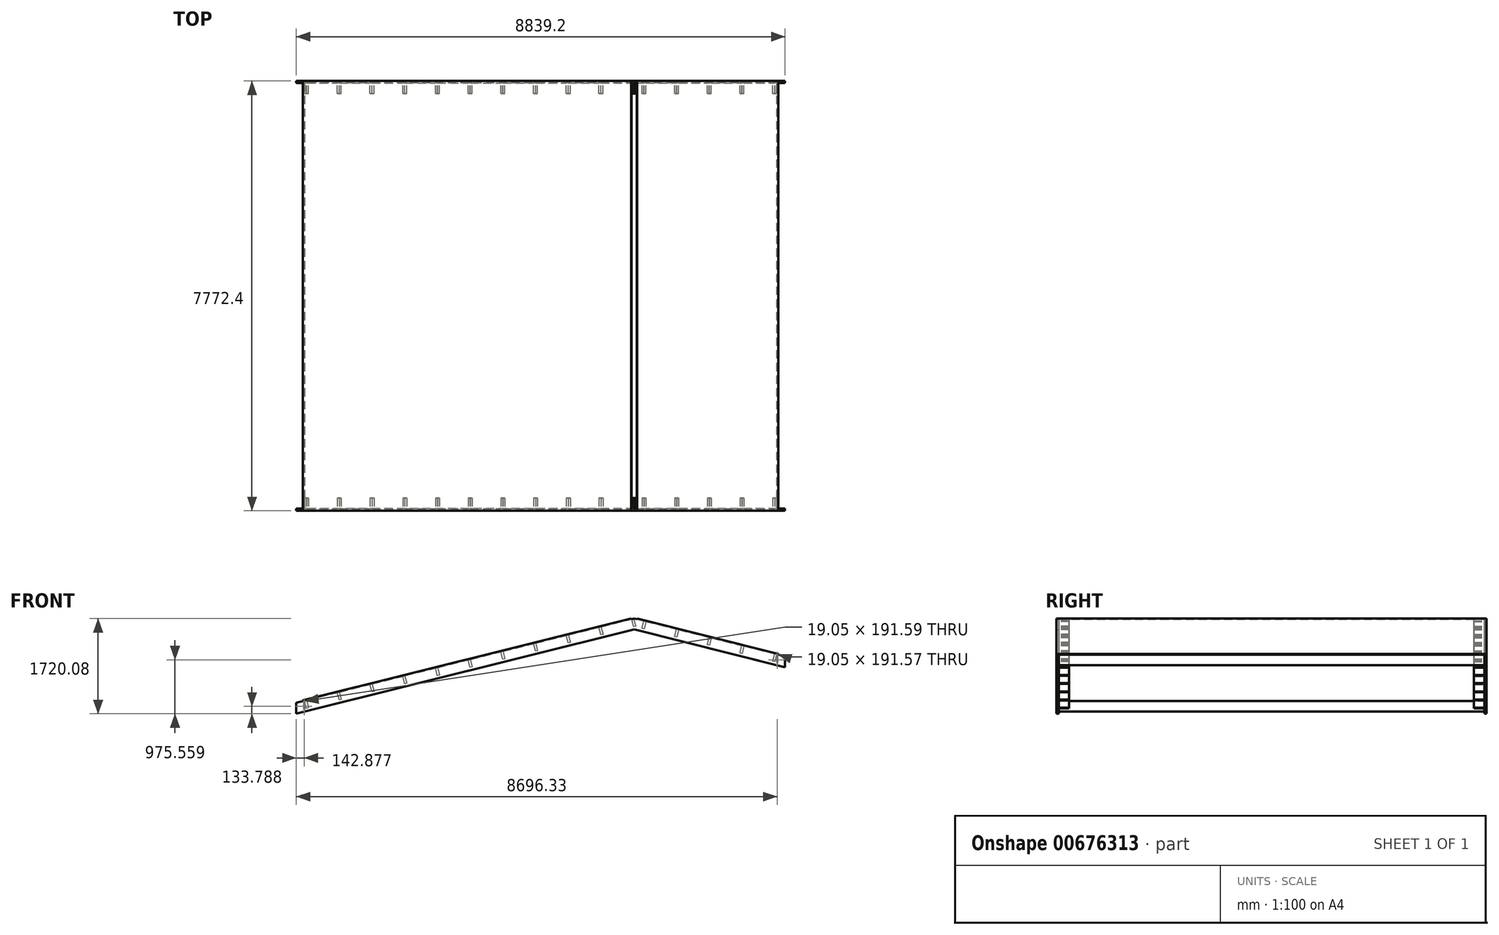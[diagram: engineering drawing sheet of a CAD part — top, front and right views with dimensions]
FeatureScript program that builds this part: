
annotation { "Feature Type Name" : "Feature", "Feature Type Description" : "" }
export const myFeature = defineFeature(function(context is Context, id is Id, definition is map)
    precondition{}
    {
        {
            var Q0;
            Q0=qCreatedBy(makeId("Front.planeOp"),FACE);
            var sketch = newSketch(context, id + "F0", { "sketchPlane" : qUnion([Q0])});
            skLineSegment(sketch, "E0", {"start": v(-6111.16, -1327.32) * mm, "end": v(0, 196.36) * mm});
            skLineSegment(sketch, "E1", {"start": v(0, 196.36) * mm, "end": v(2728.04, -485.65) * mm});
            skLineSegment(sketch, "E2", {"start": v(2728.04, -485.65) * mm, "end": v(2728.04, -682) * mm});
            skLineSegment(sketch, "E3", {"start": v(2728.04, -682) * mm, "end": v(1966.04, -491.5) * mm});
            skLineSegment(sketch, "E4", {"start": v(0, 0) * mm, "end": v(-5209.46, -1298.86) * mm});
            skLineSegment(sketch, "E5", {"start": v(-6111.16, -1523.68) * mm, "end": v(-6111.16, -1327.32) * mm});
            skLineSegment(sketch, "E6", {"start": v(0, 196.36) * mm, "end": v(0, 0) * mm, "construction": true});
            skLineSegment(sketch, "E7", {"start": v(0, 0) * mm, "end": v(46.2, 184.81) * mm, "construction": true});
            skLineSegment(sketch, "E8.trimOffspring", {"start": v(-5349.16, -1333.7) * mm, "end": v(-6111.16, -1523.68) * mm});
            skLineSegment(sketch, "E9.trimOffspring", {"start": v(1826.34, -456.58) * mm, "end": v(0, 0) * mm});
            skLineSegment(sketch, "E10", {"start": v(1966.04, -491.5) * mm, "end": v(1966.04, -456.58) * mm, "construction": true});
            skLineSegment(sketch, "E11", {"start": v(1966.04, -456.58) * mm, "end": v(1826.34, -456.58) * mm, "construction": true});
            skLineSegment(sketch, "E12", {"start": v(-5349.16, -1333.7) * mm, "end": v(-5349.16, -1298.86) * mm, "construction": true});
            skLineSegment(sketch, "E13", {"start": v(-5349.16, -1298.86) * mm, "end": v(-5209.46, -1298.86) * mm, "construction": true});
            skLineSegment(sketch, "E14.bottom", {"start": v(-5349.16, -1298.86) * mm, "end": v(-1831.26, -1298.86) * mm, "construction": true});
            skLineSegment(sketch, "E14.top", {"start": v(-5349.16, -4042.06) * mm, "end": v(-1831.26, -4042.06) * mm, "construction": true});
            skLineSegment(sketch, "E14.left", {"start": v(-5349.16, -1298.86) * mm, "end": v(-5349.16, -4042.06) * mm, "construction": true});
            skLineSegment(sketch, "E14.right", {"start": v(-1831.26, -1298.86) * mm, "end": v(-1831.26, -4042.06) * mm, "construction": true});
            skLineSegment(sketch, "E15.bottom", {"start": v(1966.04, -456.58) * mm, "end": v(-1831.26, -456.58) * mm, "construction": true});
            skLineSegment(sketch, "E15.top", {"start": v(1966.04, -4042.06) * mm, "end": v(-1831.26, -4042.06) * mm, "construction": true});
            skLineSegment(sketch, "E15.left", {"start": v(1966.04, -456.58) * mm, "end": v(1966.04, -4042.06) * mm, "construction": true});
            skLineSegment(sketch, "E15.right", {"start": v(-1831.26, -456.58) * mm, "end": v(-1831.26, -4042.06) * mm, "construction": true});
            skLineSegment(sketch, "E16", {"start": v(-5349.16, -1333.7) * mm, "end": v(-5209.46, -1298.86) * mm});
            skLineSegment(sketch, "E17", {"start": v(1826.34, -456.58) * mm, "end": v(1966.04, -491.5) * mm});
            skSolve(sketch);
        }
        {
            var Q0;
            Q0=qSketchRegion(id+"F0",true);
            extrude(context, id + "F1", {"entities" : qUnion([Q0]), "depth" : 38.1 * mm, "offsetDistance" : 25.4 * mm});
        }
        {
            var Q0;
            Q0=makeQuery(id+"F1.opExtrude","CAP_FACE",FACE,{"disambiguationData":[OSD([sQuery(id+"F0.wireOp",EDGE,"E0"),sQuery(id+"F0.wireOp",EDGE,"E1"),sQuery(id+"F0.wireOp",EDGE,"E2"),sQuery(id+"F0.wireOp",EDGE,"E3"),sQuery(id+"F0.wireOp",EDGE,"E4"),sQuery(id+"F0.wireOp",EDGE,"E5"),sQuery(id+"F0.wireOp",EDGE,"E8.trimOffspring"),sQuery(id+"F0.wireOp",EDGE,"E9.trimOffspring"),sQuery(id+"F0.wireOp",EDGE,"E16"),sQuery(id+"F0.wireOp",EDGE,"E17")])],"isStart":true});
            var sketch = newSketch(context, id + "F2", { "sketchPlane" : qUnion([Q0])});
            skLineSegment(sketch, "E18.bottom", {"start": v(5977.8, -1294.1) * mm, "end": v(5958.76, -1294.1) * mm});
            skLineSegment(sketch, "E18.top", {"start": v(5977.8, -1485.69) * mm, "end": v(5958.76, -1485.69) * mm});
            skLineSegment(sketch, "E18.left", {"start": v(5977.8, -1294.1) * mm, "end": v(5977.8, -1485.69) * mm});
            skLineSegment(sketch, "E18.right", {"start": v(5958.76, -1294.1) * mm, "end": v(5958.76, -1485.69) * mm});
            skLineSegment(sketch, "E19.bottom", {"start": v(-2594.7, -452.33) * mm, "end": v(-2575.64, -452.33) * mm});
            skLineSegment(sketch, "E19.top", {"start": v(-2594.7, -643.9) * mm, "end": v(-2575.64, -643.9) * mm});
            skLineSegment(sketch, "E19.left", {"start": v(-2594.7, -452.33) * mm, "end": v(-2594.7, -643.9) * mm});
            skLineSegment(sketch, "E19.right", {"start": v(-2575.64, -452.33) * mm, "end": v(-2575.64, -643.9) * mm});
            skLineSegment(sketch, "E20", {"start": v(-2576.52, -447.77) * mm, "end": v(-2542.64, -583.3) * mm});
            skLineSegment(sketch, "E21", {"start": v(-2542.64, -583.3) * mm, "end": v(-2505.68, -574.05) * mm});
            skLineSegment(sketch, "E22", {"start": v(-2505.68, -574.05) * mm, "end": v(-2539.56, -438.52) * mm});
            skLineSegment(sketch, "E23", {"start": v(-2539.56, -438.52) * mm, "end": v(-2576.52, -447.77) * mm});
            skLineSegment(sketch, "E24.1.0.0", {"start": v(-1914.28, -426.2) * mm, "end": v(-1948.16, -290.68) * mm});
            skLineSegment(sketch, "E24.1.0.1", {"start": v(-1951.24, -435.45) * mm, "end": v(-1914.28, -426.2) * mm});
            skLineSegment(sketch, "E24.1.0.2", {"start": v(-1985.12, -299.92) * mm, "end": v(-1951.24, -435.45) * mm});
            skLineSegment(sketch, "E24.1.0.3", {"start": v(-1948.16, -290.68) * mm, "end": v(-1985.12, -299.92) * mm});
            skLineSegment(sketch, "E24.2.0.0", {"start": v(-1322.88, -278.36) * mm, "end": v(-1356.76, -142.83) * mm});
            skLineSegment(sketch, "E24.2.0.1", {"start": v(-1359.84, -287.6) * mm, "end": v(-1322.88, -278.36) * mm});
            skLineSegment(sketch, "E24.2.0.2", {"start": v(-1393.72, -152.07) * mm, "end": v(-1359.84, -287.6) * mm});
            skLineSegment(sketch, "E24.2.0.3", {"start": v(-1356.76, -142.83) * mm, "end": v(-1393.72, -152.07) * mm});
            skLineSegment(sketch, "E24.3.0.0", {"start": v(-731.48, -130.5) * mm, "end": v(-765.36, 5.02) * mm});
            skLineSegment(sketch, "E24.3.0.1", {"start": v(-768.44, -139.75) * mm, "end": v(-731.48, -130.5) * mm});
            skLineSegment(sketch, "E24.3.0.2", {"start": v(-802.33, -4.22) * mm, "end": v(-768.44, -139.75) * mm});
            skLineSegment(sketch, "E24.3.0.3", {"start": v(-765.36, 5.02) * mm, "end": v(-802.33, -4.22) * mm});
            skLineSegment(sketch, "E24.4.0.0", {"start": v(-140.08, 17.34) * mm, "end": v(-173.96, 152.87) * mm});
            skLineSegment(sketch, "E24.4.0.1", {"start": v(-177.04, 8.1) * mm, "end": v(-140.08, 17.34) * mm});
            skLineSegment(sketch, "E24.4.0.2", {"start": v(-210.93, 143.63) * mm, "end": v(-177.04, 8.1) * mm});
            skLineSegment(sketch, "E24.4.0.3", {"start": v(-173.96, 152.87) * mm, "end": v(-210.93, 143.63) * mm});
            skLineSegment(sketch, "E24.direction1", {"start": v(-2542.64, -583.3) * mm, "end": v(-1951.24, -435.45) * mm, "construction": true});
            skLineSegment(sketch, "E25", {"start": v(5922.66, -1280.32) * mm, "end": v(5888.87, -1415.87) * mm});
            skLineSegment(sketch, "E26", {"start": v(5888.87, -1415.87) * mm, "end": v(5925.84, -1425.1) * mm});
            skLineSegment(sketch, "E27", {"start": v(5925.84, -1425.1) * mm, "end": v(5959.63, -1289.54) * mm});
            skLineSegment(sketch, "E28", {"start": v(5959.63, -1289.54) * mm, "end": v(5922.66, -1280.32) * mm});
            skLineSegment(sketch, "E29.1.0.0", {"start": v(5368.14, -1142.06) * mm, "end": v(5331.17, -1132.85) * mm});
            skLineSegment(sketch, "E29.1.0.1", {"start": v(5334.34, -1277.62) * mm, "end": v(5368.14, -1142.06) * mm});
            skLineSegment(sketch, "E29.1.0.2", {"start": v(5297.38, -1268.4) * mm, "end": v(5334.34, -1277.62) * mm});
            skLineSegment(sketch, "E29.1.0.3", {"start": v(5331.17, -1132.85) * mm, "end": v(5297.38, -1268.4) * mm});
            skLineSegment(sketch, "E29.2.0.0", {"start": v(4776.65, -994.59) * mm, "end": v(4739.68, -985.37) * mm});
            skLineSegment(sketch, "E29.2.0.1", {"start": v(4742.85, -1130.14) * mm, "end": v(4776.65, -994.59) * mm});
            skLineSegment(sketch, "E29.2.0.2", {"start": v(4705.88, -1120.92) * mm, "end": v(4742.85, -1130.14) * mm});
            skLineSegment(sketch, "E29.2.0.3", {"start": v(4739.68, -985.37) * mm, "end": v(4705.88, -1120.92) * mm});
            skLineSegment(sketch, "E29.3.0.0", {"start": v(4185.16, -847.11) * mm, "end": v(4148.19, -837.9) * mm});
            skLineSegment(sketch, "E29.3.0.1", {"start": v(4151.36, -982.66) * mm, "end": v(4185.16, -847.11) * mm});
            skLineSegment(sketch, "E29.3.0.2", {"start": v(4114.4, -973.45) * mm, "end": v(4151.36, -982.66) * mm});
            skLineSegment(sketch, "E29.3.0.3", {"start": v(4148.19, -837.9) * mm, "end": v(4114.4, -973.45) * mm});
            skLineSegment(sketch, "E29.4.0.0", {"start": v(3593.66, -699.64) * mm, "end": v(3556.7, -690.42) * mm});
            skLineSegment(sketch, "E29.4.0.1", {"start": v(3559.87, -835.19) * mm, "end": v(3593.66, -699.64) * mm});
            skLineSegment(sketch, "E29.4.0.2", {"start": v(3522.9, -825.97) * mm, "end": v(3559.87, -835.19) * mm});
            skLineSegment(sketch, "E29.4.0.3", {"start": v(3556.7, -690.42) * mm, "end": v(3522.9, -825.97) * mm});
            skLineSegment(sketch, "E29.5.0.0", {"start": v(3002.17, -552.16) * mm, "end": v(2965.2, -542.95) * mm});
            skLineSegment(sketch, "E29.5.0.1", {"start": v(2968.38, -687.71) * mm, "end": v(3002.17, -552.16) * mm});
            skLineSegment(sketch, "E29.5.0.2", {"start": v(2931.4, -678.5) * mm, "end": v(2968.38, -687.71) * mm});
            skLineSegment(sketch, "E29.5.0.3", {"start": v(2965.2, -542.95) * mm, "end": v(2931.4, -678.5) * mm});
            skLineSegment(sketch, "E29.6.0.0", {"start": v(2410.68, -404.69) * mm, "end": v(2373.71, -395.47) * mm});
            skLineSegment(sketch, "E29.6.0.1", {"start": v(2376.88, -540.24) * mm, "end": v(2410.68, -404.69) * mm});
            skLineSegment(sketch, "E29.6.0.2", {"start": v(2339.91, -531.02) * mm, "end": v(2376.88, -540.24) * mm});
            skLineSegment(sketch, "E29.6.0.3", {"start": v(2373.71, -395.47) * mm, "end": v(2339.91, -531.02) * mm});
            skLineSegment(sketch, "E29.7.0.0", {"start": v(1819.19, -257.21) * mm, "end": v(1782.22, -248) * mm});
            skLineSegment(sketch, "E29.7.0.1", {"start": v(1785.4, -392.76) * mm, "end": v(1819.19, -257.21) * mm});
            skLineSegment(sketch, "E29.7.0.2", {"start": v(1748.42, -383.54) * mm, "end": v(1785.4, -392.76) * mm});
            skLineSegment(sketch, "E29.7.0.3", {"start": v(1782.22, -248) * mm, "end": v(1748.42, -383.54) * mm});
            skLineSegment(sketch, "E29.8.0.0", {"start": v(1227.7, -109.74) * mm, "end": v(1190.73, -100.52) * mm});
            skLineSegment(sketch, "E29.8.0.1", {"start": v(1193.9, -245.29) * mm, "end": v(1227.7, -109.74) * mm});
            skLineSegment(sketch, "E29.8.0.2", {"start": v(1156.93, -236.07) * mm, "end": v(1193.9, -245.29) * mm});
            skLineSegment(sketch, "E29.8.0.3", {"start": v(1190.73, -100.52) * mm, "end": v(1156.93, -236.07) * mm});
            skLineSegment(sketch, "E29.9.0.0", {"start": v(636.2, 37.74) * mm, "end": v(599.23, 46.96) * mm});
            skLineSegment(sketch, "E29.9.0.1", {"start": v(602.4, -97.81) * mm, "end": v(636.2, 37.74) * mm});
            skLineSegment(sketch, "E29.9.0.2", {"start": v(565.44, -88.6) * mm, "end": v(602.4, -97.81) * mm});
            skLineSegment(sketch, "E29.9.0.3", {"start": v(599.23, 46.96) * mm, "end": v(565.44, -88.6) * mm});
            skLineSegment(sketch, "E29.10.0.0", {"start": v(44.71, 185.22) * mm, "end": v(7.74, 194.43) * mm});
            skLineSegment(sketch, "E29.10.0.1", {"start": v(10.91, 49.67) * mm, "end": v(44.71, 185.22) * mm});
            skLineSegment(sketch, "E29.10.0.2", {"start": v(-26.05, 58.88) * mm, "end": v(10.91, 49.67) * mm});
            skLineSegment(sketch, "E29.10.0.3", {"start": v(7.74, 194.43) * mm, "end": v(-26.05, 58.88) * mm});
            skLineSegment(sketch, "E29.direction1", {"start": v(5888.87, -1415.87) * mm, "end": v(5297.38, -1268.4) * mm, "construction": true});
            skSolve(sketch);
        }
        {
            var Q0;
            Q0 = qSketchRegion(id + "F2", true);
            extrude(context, id + "F3", {"entities" : qUnion([Q0]), "operationType" : NewBodyOperationType.ADD, "depth" : 190.5 * mm, "offsetDistance" : 25.4 * mm});
        }
        {
            var Q0;
            Q0=makeQuery(id+"F3.opExtrude","CAP_FACE",FACE,{"disambiguationData":[OSD([sQuery(id+"F2.wireOp",EDGE,"E18.bottom"),sQuery(id+"F2.wireOp",EDGE,"E18.top"),sQuery(id+"F2.wireOp",EDGE,"E18.left"),sQuery(id+"F2.wireOp",EDGE,"E18.right")])],"isStart":false});
            var sketch = newSketch(context, id + "F4", { "sketchPlane" : qUnion([Q0])});
            skLineSegment(sketch, "E30.bottom", {"start": v(5958.76, -1294.1) * mm, "end": v(5977.8, -1294.1) * mm});
            skLineSegment(sketch, "E30.top", {"start": v(5958.76, -1485.69) * mm, "end": v(5977.8, -1485.69) * mm});
            skLineSegment(sketch, "E30.left", {"start": v(5958.76, -1294.1) * mm, "end": v(5958.76, -1485.69) * mm});
            skLineSegment(sketch, "E30.right", {"start": v(5977.8, -1294.1) * mm, "end": v(5977.8, -1485.69) * mm});
            skLineSegment(sketch, "E31.bottom", {"start": v(-2594.7, -452.33) * mm, "end": v(-2575.64, -452.33) * mm});
            skLineSegment(sketch, "E31.top", {"start": v(-2594.7, -643.9) * mm, "end": v(-2575.64, -643.9) * mm});
            skLineSegment(sketch, "E31.left", {"start": v(-2594.7, -452.33) * mm, "end": v(-2594.7, -643.9) * mm});
            skLineSegment(sketch, "E31.right", {"start": v(-2575.64, -452.33) * mm, "end": v(-2575.64, -643.9) * mm});
            skSolve(sketch);
        }
        {
            var Q0;
            Q0 = qSketchRegion(id + "F4", true);
            extrude(context, id + "F5", {"entities" : qUnion([Q0]), "operationType" : NewBodyOperationType.ADD, "depth" : 3657.6 * mm, "offsetDistance" : 25.4 * mm});
        }
        {
            var Q0;
            Q0=makeQuery(id+"F3.boolean.opBoolean","MERGE",FACE,{"derivedFrom":[makeQuery(id+"F1.opExtrude","SWEPT_FACE",FACE,{"disambiguationData":[OSD([sQuery(id+"F0.wireOp",EDGE,"E1")])]}),makeQuery(id+"F3.opExtrude","SWEPT_FACE",FACE,{"disambiguationData":[OSD([sQuery(id+"F2.wireOp",EDGE,"E23")])]}),makeQuery(id+"F3.opExtrude","SWEPT_FACE",FACE,{"disambiguationData":[OSD([sQuery(id+"F2.wireOp",EDGE,"E24.1.0.3")])]}),makeQuery(id+"F3.opExtrude","SWEPT_FACE",FACE,{"disambiguationData":[OSD([sQuery(id+"F2.wireOp",EDGE,"E24.2.0.3")])]}),makeQuery(id+"F3.opExtrude","SWEPT_FACE",FACE,{"disambiguationData":[OSD([sQuery(id+"F2.wireOp",EDGE,"E24.3.0.3")])]}),makeQuery(id+"F3.opExtrude","SWEPT_FACE",FACE,{"disambiguationData":[OSD([sQuery(id+"F2.wireOp",EDGE,"E24.4.0.3")])]})]});
            var sketch = newSketch(context, id + "F6", { "sketchPlane" : qUnion([Q0])});
            skLineSegment(sketch, "E32.bottom", {"start": v(3.18, -38.1) * mm, "end": v(2637.38, -38.1) * mm});
            skLineSegment(sketch, "E32.top", {"start": v(3.18, 3848.1) * mm, "end": v(2637.38, 3848.1) * mm});
            skLineSegment(sketch, "E32.left", {"start": v(3.18, -38.1) * mm, "end": v(3.18, 3848.1) * mm});
            skLineSegment(sketch, "E32.right", {"start": v(2637.38, -38.1) * mm, "end": v(2637.38, 3848.1) * mm});
            skSolve(sketch);
        }
        {
            var Q0;
            Q0 = qSketchRegion(id + "F6", true);
            extrude(context, id + "F7", {"entities" : qUnion([Q0]), "operationType" : NewBodyOperationType.ADD, "depth" : 12.7 * mm, "offsetDistance" : 25.4 * mm});
        }
        {
            var Q0;
            Q0=makeQuery(id+"F3.boolean.opBoolean","MERGE",FACE,{"derivedFrom":[makeQuery(id+"F1.opExtrude","SWEPT_FACE",FACE,{"disambiguationData":[OSD([sQuery(id+"F0.wireOp",EDGE,"E0")])]}),makeQuery(id+"F3.opExtrude","SWEPT_FACE",FACE,{"disambiguationData":[OSD([sQuery(id+"F2.wireOp",EDGE,"E28")])]}),makeQuery(id+"F3.opExtrude","SWEPT_FACE",FACE,{"disambiguationData":[OSD([sQuery(id+"F2.wireOp",EDGE,"E29.1.0.0")])]}),makeQuery(id+"F3.opExtrude","SWEPT_FACE",FACE,{"disambiguationData":[OSD([sQuery(id+"F2.wireOp",EDGE,"E29.2.0.0")])]}),makeQuery(id+"F3.opExtrude","SWEPT_FACE",FACE,{"disambiguationData":[OSD([sQuery(id+"F2.wireOp",EDGE,"E29.3.0.0")])]}),makeQuery(id+"F3.opExtrude","SWEPT_FACE",FACE,{"disambiguationData":[OSD([sQuery(id+"F2.wireOp",EDGE,"E29.4.0.0")])]}),makeQuery(id+"F3.opExtrude","SWEPT_FACE",FACE,{"disambiguationData":[OSD([sQuery(id+"F2.wireOp",EDGE,"E29.5.0.0")])]}),makeQuery(id+"F3.opExtrude","SWEPT_FACE",FACE,{"disambiguationData":[OSD([sQuery(id+"F2.wireOp",EDGE,"E29.6.0.0")])]}),makeQuery(id+"F3.opExtrude","SWEPT_FACE",FACE,{"disambiguationData":[OSD([sQuery(id+"F2.wireOp",EDGE,"E29.7.0.0")])]}),makeQuery(id+"F3.opExtrude","SWEPT_FACE",FACE,{"disambiguationData":[OSD([sQuery(id+"F2.wireOp",EDGE,"E29.8.0.0")])]}),makeQuery(id+"F3.opExtrude","SWEPT_FACE",FACE,{"disambiguationData":[OSD([sQuery(id+"F2.wireOp",EDGE,"E29.9.0.0")])]}),makeQuery(id+"F3.opExtrude","SWEPT_FACE",FACE,{"disambiguationData":[OSD([sQuery(id+"F2.wireOp",EDGE,"E29.10.0.0")])]})]});
            var sketch = newSketch(context, id + "F8", { "sketchPlane" : qUnion([Q0])});
            skLineSegment(sketch, "E33.bottom", {"start": v(-3.3, -38.1) * mm, "end": v(-6123.74, -38.1) * mm});
            skLineSegment(sketch, "E33.top", {"start": v(-3.3, 3848.1) * mm, "end": v(-6123.74, 3848.1) * mm});
            skLineSegment(sketch, "E33.left", {"start": v(-3.3, -38.1) * mm, "end": v(-3.3, 3848.1) * mm});
            skLineSegment(sketch, "E33.right", {"start": v(-6123.74, -38.1) * mm, "end": v(-6123.74, 3848.1) * mm});
            skSolve(sketch);
        }
        {
            var Q0;
            Q0 = qSketchRegion(id + "F8", true);
            extrude(context, id + "F9", {"entities" : qUnion([Q0]), "operationType" : NewBodyOperationType.ADD, "depth" : 12.7 * mm, "offsetDistance" : 25.4 * mm});
        }
        {
            var Q0;
            Q0=makeQuery(id+"F1.opExtrude","SWEPT_BODY",BODY,{"disambiguationData":[OSD([sQuery(id+"F0.wireOp",EDGE,"E0"),sQuery(id+"F0.wireOp",EDGE,"E1"),sQuery(id+"F0.wireOp",EDGE,"E2"),sQuery(id+"F0.wireOp",EDGE,"E3"),sQuery(id+"F0.wireOp",EDGE,"E4"),sQuery(id+"F0.wireOp",EDGE,"E5"),sQuery(id+"F0.wireOp",EDGE,"E8.trimOffspring"),sQuery(id+"F0.wireOp",EDGE,"E9.trimOffspring"),sQuery(id+"F0.wireOp",EDGE,"E16"),sQuery(id+"F0.wireOp",EDGE,"E17")])]});
            var Q1;
            Q1=makeQuery(id+"F7.opExtrude","SWEPT_FACE",FACE,{"disambiguationData":[OSD([sQuery(id+"F6.wireOp",EDGE,"E32.top")])]});
            mirror(context, id + "F10", {"operationType" : NewBodyOperationType.ADD, "entities" : qUnion([Q0]), "mirrorPlane" : qUnion([Q1])});
        }
    });
